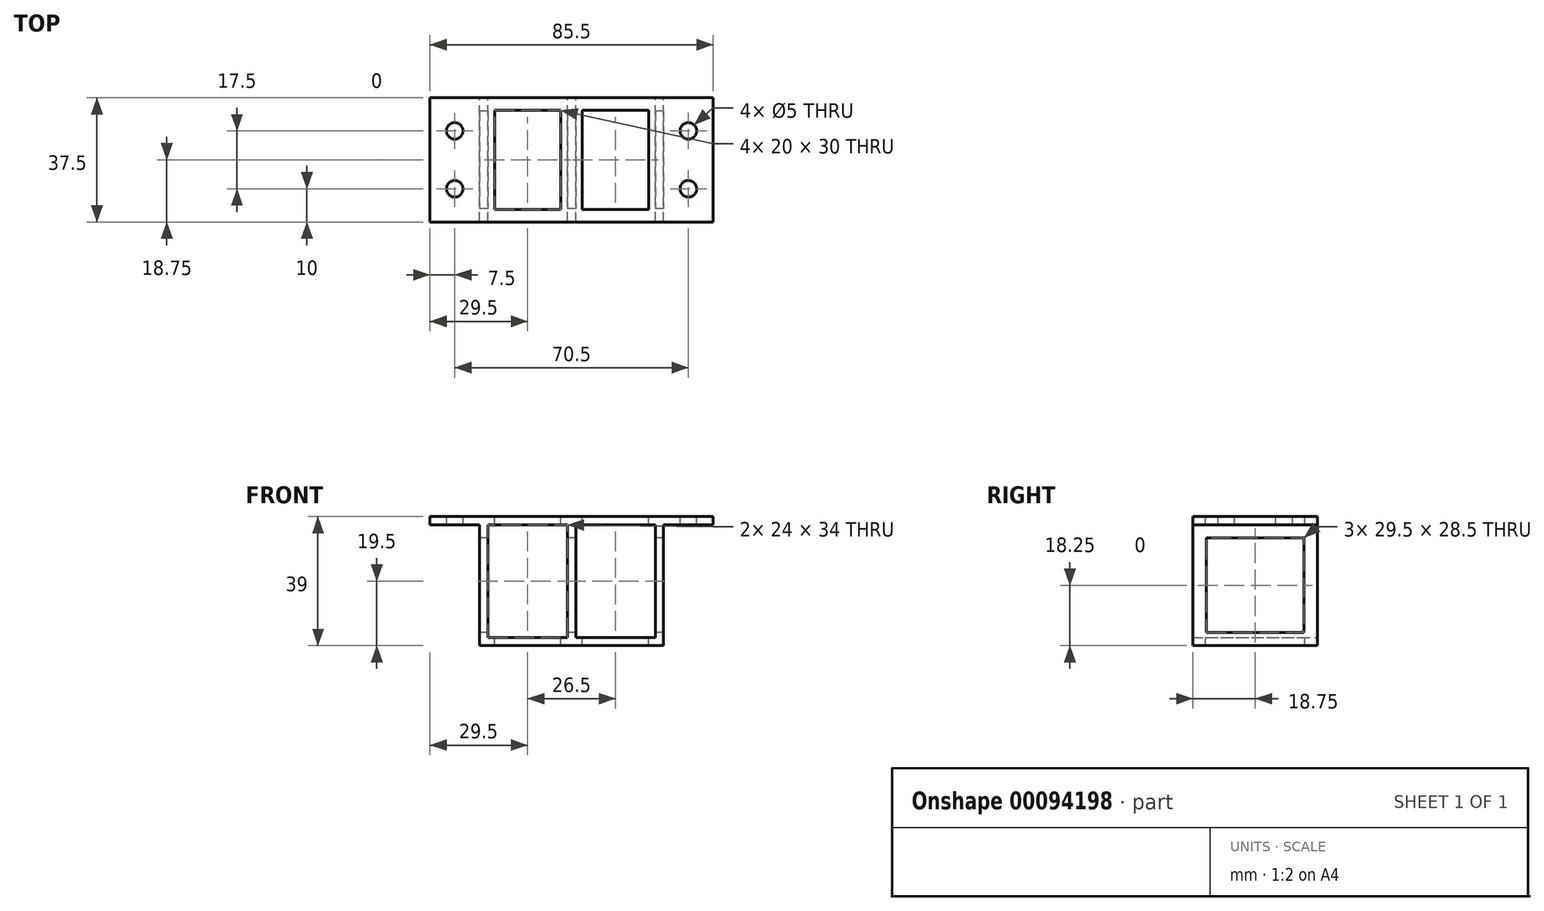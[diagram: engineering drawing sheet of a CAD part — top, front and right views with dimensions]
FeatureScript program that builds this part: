
annotation { "Feature Type Name" : "Feature", "Feature Type Description" : "" }
export const myFeature = defineFeature(function(context is Context, id is Id, definition is map)
    precondition{}
    {
        {
            var Q0;
            Q0=qCreatedBy(makeId("Front.planeOp"),FACE);
            var sketch = newSketch(context, id + "F0", { "sketchPlane" : qUnion([Q0])});
            skLineSegment(sketch, "E0.bottom", {"start": v(-12, 17) * mm, "end": v(12, 17) * mm});
            skLineSegment(sketch, "E0.top", {"start": v(-12, -17) * mm, "end": v(12, -17) * mm});
            skLineSegment(sketch, "E0.left", {"start": v(-12, 17) * mm, "end": v(-12, -17) * mm});
            skLineSegment(sketch, "E0.right", {"start": v(12, 17) * mm, "end": v(12, -17) * mm});
            skPoint(sketch, "E0.middle", {"position": v(0, 0) * mm});
            skLineSegment(sketch, "E1.bottom", {"start": v(-14.5, 19.5) * mm, "end": v(14.5, 19.5) * mm});
            skLineSegment(sketch, "E1.top", {"start": v(-14.5, -19.5) * mm, "end": v(14.5, -19.5) * mm});
            skLineSegment(sketch, "E1.left", {"start": v(-14.5, 19.5) * mm, "end": v(-14.5, -19.5) * mm});
            skLineSegment(sketch, "E2.MirrorCS", {"start": v(14.5, 17) * mm, "end": v(14.5, -17) * mm});
            skLineSegment(sketch, "E3.MirrorCS", {"start": v(38.5, 17) * mm, "end": v(14.5, 17) * mm});
            skLineSegment(sketch, "E4.MirrorCS", {"start": v(38.5, -17) * mm, "end": v(14.5, -17) * mm});
            skLineSegment(sketch, "E5.MirrorCS", {"start": v(38.5, 17) * mm, "end": v(38.5, -17) * mm});
            skLineSegment(sketch, "E6.MirrorCS", {"start": v(41, 19.5) * mm, "end": v(14.5, 19.5) * mm});
            skLineSegment(sketch, "E7.MirrorCS", {"start": v(41, -19.5) * mm, "end": v(14.5, -19.5) * mm});
            skLineSegment(sketch, "E8.MirrorCS", {"start": v(41, 17) * mm, "end": v(41, -17) * mm});
            skLineSegment(sketch, "E9", {"start": v(41, 17) * mm, "end": v(41, 19.5) * mm});
            skLineSegment(sketch, "E10", {"start": v(41, 19.5) * mm, "end": v(41, -19.5) * mm});
            skSolve(sketch);
        }
        {
            var Q0;
            Q0=qSketchRegion(id+"F0",true);
            extrude(context, id + "F1", {"entities" : qUnion([Q0]), "depth" : 18.75 * mm, "hasSecondDirection" : true, "secondDirectionOppositeDirection" : true, "secondDirectionDepth" : 18.75 * mm});
        }
        {
            var Q0;
            Q0=makeQuery(id+"F1.opExtrude","SWEPT_FACE",FACE,{"disambiguationData":[OSD([sQuery(id+"F0.wireOp",EDGE,"E1.bottom")])]});
            var sketch = newSketch(context, id + "F2", { "sketchPlane" : qUnion([Q0])});
            skPoint(sketch, "E11.0.end.orphan", {"position": v(-14.5, -18.75) * mm});
            skPoint(sketch, "E12.bottom.start.orphan", {"position": v(-14.5, 18.75) * mm});
            skPoint(sketch, "E12.top.end.orphan", {"position": v(-29.5, -18.75) * mm});
            skPoint(sketch, "E13.right.end.orphan", {"position": v(56, -18.75) * mm});
            skLineSegment(sketch, "E14.bottom", {"start": v(-29.5, -18.75) * mm, "end": v(56, -18.75) * mm});
            skLineSegment(sketch, "E14.top", {"start": v(-29.5, 18.75) * mm, "end": v(56, 18.75) * mm});
            skLineSegment(sketch, "E14.left", {"start": v(-29.5, -18.75) * mm, "end": v(-29.5, 18.75) * mm});
            skLineSegment(sketch, "E14.right", {"start": v(56, -18.75) * mm, "end": v(56, 18.75) * mm});
            skLineSegment(sketch, "E15", {"start": v(-29.5, 18.75) * mm, "end": v(-14.5, 18.75) * mm});
            skPoint(sketch, "E16.centerSnap0", {"position": v(-22, 18.75) * mm});
            skCircle(sketch, "E17", {"center": v(-22, 8.75) * mm, "radius": 2.5 * mm});
            skCircle(sketch, "E18.MirrorC", {"center": v(-22, -8.75) * mm, "radius": 2.5 * mm});
            skLineSegment(sketch, "E19", {"start": v(13.25, 18.75) * mm, "end": v(13.25, -18.75) * mm, "construction": true});
            skCircle(sketch, "E20.MirrorC", {"center": v(48.5, 8.75) * mm, "radius": 2.5 * mm});
            skCircle(sketch, "E21.MirrorC", {"center": v(48.5, -8.75) * mm, "radius": 2.5 * mm});
            skLineSegment(sketch, "E22.bottom", {"start": v(-10, 15) * mm, "end": v(10, 15) * mm});
            skLineSegment(sketch, "E22.top", {"start": v(-10, -15) * mm, "end": v(10, -15) * mm});
            skLineSegment(sketch, "E22.left", {"start": v(-10, 15) * mm, "end": v(-10, -15) * mm});
            skLineSegment(sketch, "E22.right", {"start": v(10, 15) * mm, "end": v(10, -15) * mm});
            skPoint(sketch, "E22.middle", {"position": v(0, 0) * mm});
            skLineSegment(sketch, "E23.bottom", {"start": v(3.25, 15) * mm, "end": v(23.25, 15) * mm});
            skLineSegment(sketch, "E23.top", {"start": v(3.25, -15) * mm, "end": v(23.25, -15) * mm});
            skLineSegment(sketch, "E23.left", {"start": v(3.25, 15) * mm, "end": v(3.25, -15) * mm});
            skLineSegment(sketch, "E23.right", {"start": v(23.25, 15) * mm, "end": v(23.25, -15) * mm});
            skPoint(sketch, "E23.middle", {"position": v(13.25, 0) * mm});
            skLineSegment(sketch, "E24.MirrorCS", {"start": v(36.5, 15) * mm, "end": v(16.5, 15) * mm});
            skLineSegment(sketch, "E25.MirrorCS", {"start": v(16.5, 15) * mm, "end": v(16.5, -15) * mm});
            skLineSegment(sketch, "E26.MirrorCS", {"start": v(36.5, -15) * mm, "end": v(16.5, -15) * mm});
            skLineSegment(sketch, "E27.MirrorCS", {"start": v(36.5, 15) * mm, "end": v(36.5, -15) * mm});
            skSolve(sketch);
        }
        {
            var Q0;
            Q0=qSketchRegion(id+"F2",true);
            extrude(context, id + "F3", {"entities" : qUnion([Q0]), "operationType" : NewBodyOperationType.ADD, "oppositeDirection" : true, "depth" : 2.5 * mm});
        }
        {
            var Q0;
            {var subQ0=sQuery(id+"F2.wireOp",EDGE,"E22.right");Q0=makeQuery(id+"F2.imprint","IMPRINT",FACE,{"disambiguationData":[TD([[makeQuery(id+"F2.imprint","IMPRINT",EDGE,{"derivedFrom":subQ0}),-1.0]])]});}
            var Q1;
            Q1=makeQuery(id+"F2.imprint","IMPRINT",FACE,{"disambiguationData":[TD([[makeQuery(id+"F2.imprint","IMPRINT",EDGE,{"derivedFrom":sQuery(id+"F2.wireOp",EDGE,"E22.bottom")}),-1.0]])]});
            var Q2;
            {var subQ0=sQuery(id+"F2.wireOp",EDGE,"E23.right");Q2=makeQuery(id+"F2.imprint","IMPRINT",FACE,{"disambiguationData":[TD([[makeQuery(id+"F2.imprint","IMPRINT",EDGE,{"derivedFrom":subQ0}),-1.0]])]});}
            var Q3;
            {var subQ0=sQuery(id+"F2.wireOp",EDGE,"E23.right");Q3=makeQuery(id+"F2.imprint","IMPRINT",FACE,{"disambiguationData":[TD([[makeQuery(id+"F2.imprint","IMPRINT",EDGE,{"derivedFrom":subQ0}),1.0]])]});}
            extrude(context, id + "F4", {"entities" : qUnion([Q0, Q1, Q2, Q3]), "operationType" : NewBodyOperationType.REMOVE, "oppositeDirection" : true, "depth" : 60 * mm});
        }
        {
            var Q0;
            Q0=qCreatedBy(makeId("Right.planeOp"),FACE);
            var sketch = newSketch(context, id + "F5", { "sketchPlane" : qUnion([Q0])});
            skLineSegment(sketch, "E28.bottom", {"start": v(-14.75, 13) * mm, "end": v(14.75, 13) * mm});
            skLineSegment(sketch, "E28.top", {"start": v(-14.75, -15.5) * mm, "end": v(14.75, -15.5) * mm});
            skLineSegment(sketch, "E28.left", {"start": v(-14.75, 13) * mm, "end": v(-14.75, -15.5) * mm});
            skLineSegment(sketch, "E28.right", {"start": v(14.75, 13) * mm, "end": v(14.75, -15.5) * mm});
            skSolve(sketch);
        }
        {
            var Q0;
            Q0=qSketchRegion(id+"F5",true);
            extrude(context, id + "F6", {"entities" : qUnion([Q0]), "operationType" : NewBodyOperationType.REMOVE, "depth" : 76.16 * mm, "hasSecondDirection" : true, "secondDirectionOppositeDirection" : true, "secondDirectionDepth" : 25 * mm});
        }
    });
